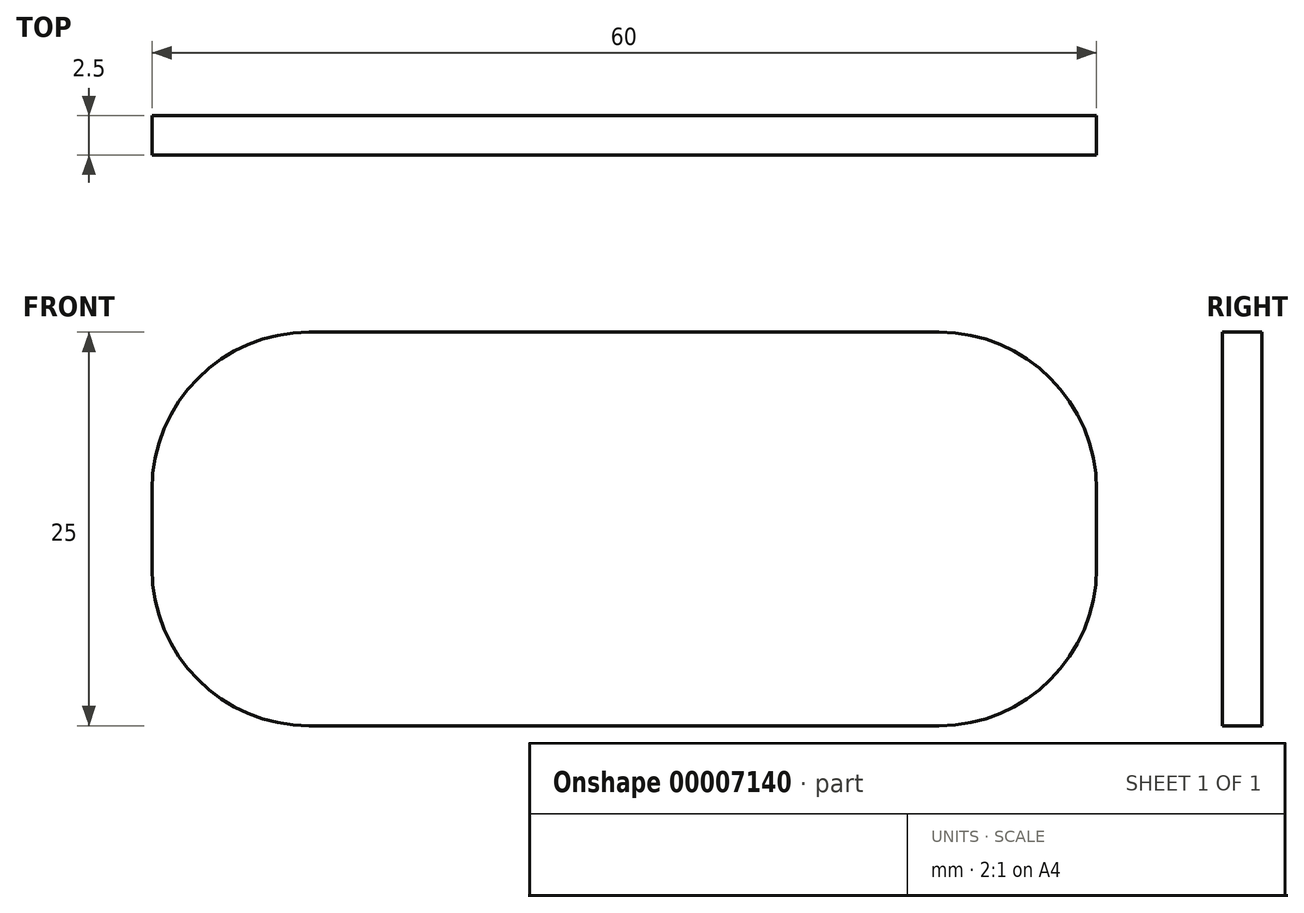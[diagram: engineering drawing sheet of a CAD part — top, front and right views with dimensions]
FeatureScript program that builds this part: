
annotation { "Feature Type Name" : "Feature", "Feature Type Description" : "" }
export const myFeature = defineFeature(function(context is Context, id is Id, definition is map)
    precondition{}
    {
        {
            var Q0;
            Q0=qCreatedBy(makeId("Front.planeOp"),FACE);
            var sketch = newSketch(context, id + "F0", { "sketchPlane" : qUnion([Q0])});
            skLineSegment(sketch, "E0.rect.bottom", {"start": v(-20, -12.5) * mm, "end": v(20, -12.5) * mm});
            skLineSegment(sketch, "E0.rect.top", {"start": v(-20, 12.5) * mm, "end": v(20, 12.5) * mm});
            skLineSegment(sketch, "E0.rect.left", {"start": v(-30, -2.5) * mm, "end": v(-30, 2.5) * mm});
            skLineSegment(sketch, "E0.rect.right", {"start": v(30, -2.5) * mm, "end": v(30, 2.5) * mm});
            skPoint(sketch, "E0.rect.middle", {"position": v(0, 0) * mm});
            skPoint(sketch, "E1.visualSharp", {"position": v(-30, 12.5) * mm});
            skArc(sketch, "E1.filletArc", {"start": v(-20, 12.5) * mm, "mid": v(-27.07, 9.57) * mm, "end": v(-30, 2.5) * mm});
            skPoint(sketch, "E2.visualSharp", {"position": v(-30, -12.5) * mm});
            skArc(sketch, "E2.filletArc", {"start": v(-30, -2.5) * mm, "mid": v(-27.07, -9.57) * mm, "end": v(-20, -12.5) * mm});
            skPoint(sketch, "E3.visualSharp", {"position": v(30, -12.5) * mm});
            skArc(sketch, "E3.filletArc", {"start": v(20, -12.5) * mm, "mid": v(27.07, -9.57) * mm, "end": v(30, -2.5) * mm});
            skPoint(sketch, "E4.visualSharp", {"position": v(30, 12.5) * mm});
            skArc(sketch, "E4.filletArc", {"start": v(30, 2.5) * mm, "mid": v(27.07, 9.57) * mm, "end": v(20, 12.5) * mm});
            skSolve(sketch);
        }
        {
            var Q0;
            Q0 = qSketchRegion(id + "F0", true);
            extrude(context, id + "F1", {"entities" : qUnion([Q0]), "depth" : 2.5 * mm});
        }
    });
